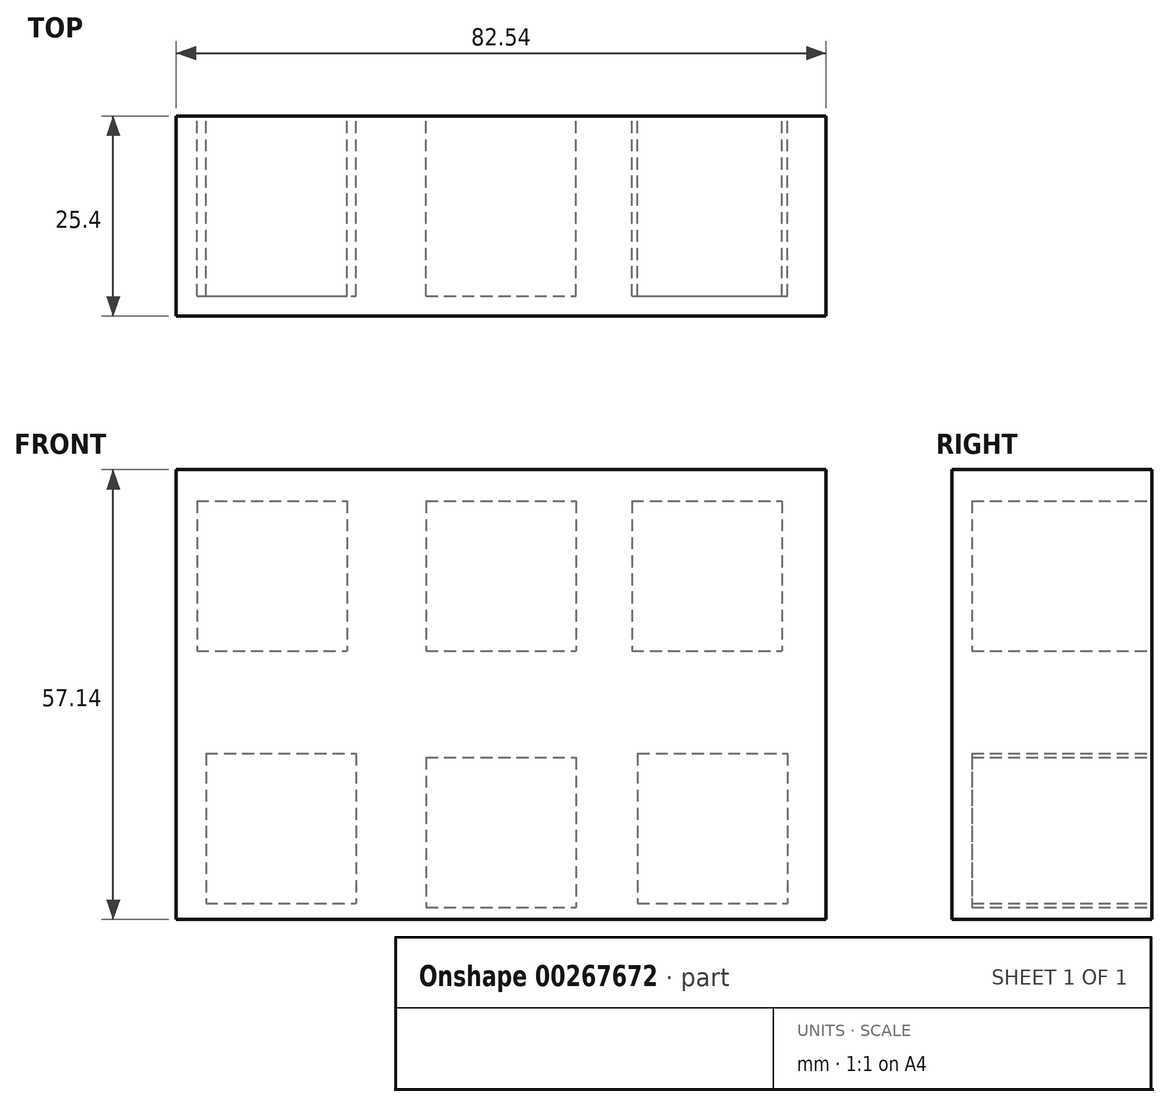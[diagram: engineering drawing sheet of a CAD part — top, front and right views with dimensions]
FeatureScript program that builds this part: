
annotation { "Feature Type Name" : "Feature", "Feature Type Description" : "" }
export const myFeature = defineFeature(function(context is Context, id is Id, definition is map)
    precondition{}
    {
        {
            var Q0;
            Q0=qCreatedBy(makeId("Front.planeOp"),FACE);
            var sketch = newSketch(context, id + "F0", { "sketchPlane" : qUnion([Q0])});
            skPoint(sketch, "E0.middle", {"position": v(0, 0) * mm});
            skLineSegment(sketch, "E1.bottom", {"start": v(38.1, 25.4) * mm, "end": v(-38.1, 25.4) * mm});
            skLineSegment(sketch, "E1.top", {"start": v(38.1, -25.4) * mm, "end": v(-38.1, -25.4) * mm});
            skLineSegment(sketch, "E1.left", {"start": v(38.1, 25.4) * mm, "end": v(38.1, -25.4) * mm});
            skLineSegment(sketch, "E1.right", {"start": v(-38.1, 25.4) * mm, "end": v(-38.1, -25.4) * mm});
            skLineSegment(sketch, "E2.bottom", {"start": v(41.28, 28.58) * mm, "end": v(-41.28, 28.57) * mm});
            skLineSegment(sketch, "E2.top", {"start": v(41.28, -28.58) * mm, "end": v(-41.28, -28.58) * mm});
            skLineSegment(sketch, "E2.left", {"start": v(41.28, 28.58) * mm, "end": v(41.28, -28.58) * mm});
            skLineSegment(sketch, "E2.right", {"start": v(-41.28, 28.58) * mm, "end": v(-41.28, -28.58) * mm});
            skSolve(sketch);
        }
        {
            var Q0;
            Q0=makeQuery(id+"F0.imprint","IMPRINT",FACE,{"disambiguationData":[TD([[makeQuery(id+"F0.imprint","IMPRINT",EDGE,{"derivedFrom":sQuery(id+"F0.wireOp",EDGE,"E1.bottom")}),-1.0]])]});
            var Q1;
            Q1=makeQuery(id+"F0.imprint","IMPRINT",FACE,{"disambiguationData":[TD([[makeQuery(id+"F0.imprint","IMPRINT",EDGE,{"derivedFrom":sQuery(id+"F0.wireOp",EDGE,"E1.bottom")}),1.0]])]});
            extrude(context, id + "F1", {"entities" : qUnion([Q0, Q1]), "depth" : 25.4 * mm});
        }
        {
            var Q0;
            Q0=qCreatedBy(makeId("Front.planeOp"),FACE);
            var sketch = newSketch(context, id + "F2", { "sketchPlane" : qUnion([Q0])});
            skLineSegment(sketch, "E3.bottom", {"start": v(16.6, 24.56) * mm, "end": v(35.65, 24.56) * mm});
            skLineSegment(sketch, "E3.top", {"start": v(16.6, 5.5) * mm, "end": v(35.65, 5.5) * mm});
            skLineSegment(sketch, "E3.left", {"start": v(16.6, 24.56) * mm, "end": v(16.6, 5.5) * mm});
            skLineSegment(sketch, "E3.right", {"start": v(35.65, 24.56) * mm, "end": v(35.65, 5.5) * mm});
            skPoint(sketch, "E3.middle", {"position": v(26.13, 15.03) * mm});
            skLineSegment(sketch, "E4.bottom", {"start": v(-9.53, 24.56) * mm, "end": v(9.53, 24.56) * mm});
            skLineSegment(sketch, "E4.top", {"start": v(-9.53, 5.5) * mm, "end": v(9.53, 5.5) * mm});
            skLineSegment(sketch, "E4.left", {"start": v(-9.53, 24.56) * mm, "end": v(-9.53, 5.5) * mm});
            skLineSegment(sketch, "E4.right", {"start": v(9.53, 24.56) * mm, "end": v(9.53, 5.5) * mm});
            skPoint(sketch, "E4.middle", {"position": v(0, 15.03) * mm});
            skLineSegment(sketch, "E5.bottom", {"start": v(-38.64, 24.56) * mm, "end": v(-19.6, 24.56) * mm});
            skLineSegment(sketch, "E5.top", {"start": v(-38.64, 5.5) * mm, "end": v(-19.6, 5.5) * mm});
            skLineSegment(sketch, "E5.left", {"start": v(-38.64, 24.56) * mm, "end": v(-38.64, 5.5) * mm});
            skLineSegment(sketch, "E5.right", {"start": v(-19.6, 24.56) * mm, "end": v(-19.6, 5.5) * mm});
            skPoint(sketch, "E5.middle", {"position": v(-29.12, 15.03) * mm});
            skLineSegment(sketch, "E6.bottom", {"start": v(17.35, -7.51) * mm, "end": v(36.4, -7.51) * mm});
            skLineSegment(sketch, "E6.top", {"start": v(17.35, -26.56) * mm, "end": v(36.4, -26.56) * mm});
            skLineSegment(sketch, "E6.left", {"start": v(17.35, -7.51) * mm, "end": v(17.35, -26.56) * mm});
            skLineSegment(sketch, "E6.right", {"start": v(36.4, -7.51) * mm, "end": v(36.4, -26.56) * mm});
            skPoint(sketch, "E6.middle", {"position": v(26.87, -17.04) * mm});
            skLineSegment(sketch, "E7.bottom", {"start": v(-9.52, -8.03) * mm, "end": v(9.53, -8.03) * mm});
            skLineSegment(sketch, "E7.top", {"start": v(-9.53, -27.08) * mm, "end": v(9.52, -27.08) * mm});
            skLineSegment(sketch, "E7.left", {"start": v(-9.52, -8.03) * mm, "end": v(-9.53, -27.08) * mm});
            skLineSegment(sketch, "E7.right", {"start": v(9.53, -8.03) * mm, "end": v(9.52, -27.08) * mm});
            skPoint(sketch, "E7.middle", {"position": v(0, -17.55) * mm});
            skLineSegment(sketch, "E8.bottom", {"start": v(-37.5, -7.51) * mm, "end": v(-18.44, -7.51) * mm});
            skLineSegment(sketch, "E8.top", {"start": v(-37.5, -26.56) * mm, "end": v(-18.44, -26.56) * mm});
            skLineSegment(sketch, "E8.left", {"start": v(-37.5, -7.51) * mm, "end": v(-37.5, -26.56) * mm});
            skLineSegment(sketch, "E8.right", {"start": v(-18.44, -7.51) * mm, "end": v(-18.44, -26.56) * mm});
            skPoint(sketch, "E8.middle", {"position": v(-27.97, -17.04) * mm});
            skSolve(sketch);
        }
        {
            var Q0;
            Q0=makeQuery(id+"F2.imprint","IMPRINT",FACE,{"disambiguationData":[TD([[makeQuery(id+"F2.imprint","IMPRINT",EDGE,{"derivedFrom":sQuery(id+"F2.wireOp",EDGE,"E3.bottom")}),-1.0]])]});
            var Q1;
            Q1=makeQuery(id+"F2.imprint","IMPRINT",FACE,{"disambiguationData":[TD([[makeQuery(id+"F2.imprint","IMPRINT",EDGE,{"derivedFrom":sQuery(id+"F2.wireOp",EDGE,"E4.bottom")}),-1.0]])]});
            var Q2;
            Q2=makeQuery(id+"F2.imprint","IMPRINT",FACE,{"disambiguationData":[TD([[makeQuery(id+"F2.imprint","IMPRINT",EDGE,{"derivedFrom":sQuery(id+"F2.wireOp",EDGE,"E5.bottom")}),-1.0]])]});
            var Q3;
            Q3=makeQuery(id+"F2.imprint","IMPRINT",FACE,{"disambiguationData":[TD([[makeQuery(id+"F2.imprint","IMPRINT",EDGE,{"derivedFrom":sQuery(id+"F2.wireOp",EDGE,"E8.bottom")}),-1.0]])]});
            var Q4;
            Q4=makeQuery(id+"F2.imprint","IMPRINT",FACE,{"disambiguationData":[TD([[makeQuery(id+"F2.imprint","IMPRINT",EDGE,{"derivedFrom":sQuery(id+"F2.wireOp",EDGE,"E7.bottom")}),-1.0]])]});
            var Q5;
            Q5=makeQuery(id+"F2.imprint","IMPRINT",FACE,{"disambiguationData":[TD([[makeQuery(id+"F2.imprint","IMPRINT",EDGE,{"derivedFrom":sQuery(id+"F2.wireOp",EDGE,"E6.bottom")}),-1.0]])]});
            extrude(context, id + "F3", {"entities" : qUnion([Q0, Q1, Q2, Q3, Q4, Q5]), "operationType" : NewBodyOperationType.REMOVE, "depth" : 22.86 * mm});
        }
    });
